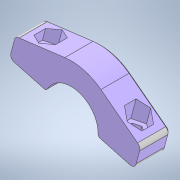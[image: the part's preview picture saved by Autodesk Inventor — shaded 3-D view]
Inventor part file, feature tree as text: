
AUTODESK INVENTOR PART (.ipt)
format: ipt  version: 2021.2 (Build 252289000, 289)  size: 246,784 bytes
history: native  units: mm
features: other x4, fillet x1, chamfer x1
ambient origin geometry x8: Origin, YZ Plane, XZ Plane, XY Plane, X Axis, Y Axis, Z Axis, Center Point
bodies: Body1 (feature_tree)
feature tree (6):
  other  "Твёрдое тело.ipt"
  fillet  "Сопряжение2"  Radius=10.0mm
  chamfer  "Фаска2"  Distance=1.0mm
  other  "Скобка 1::Твёрдое тело.ipt"
  other  "Элемент создания тегов1"
  other  "Твердое тело1"
